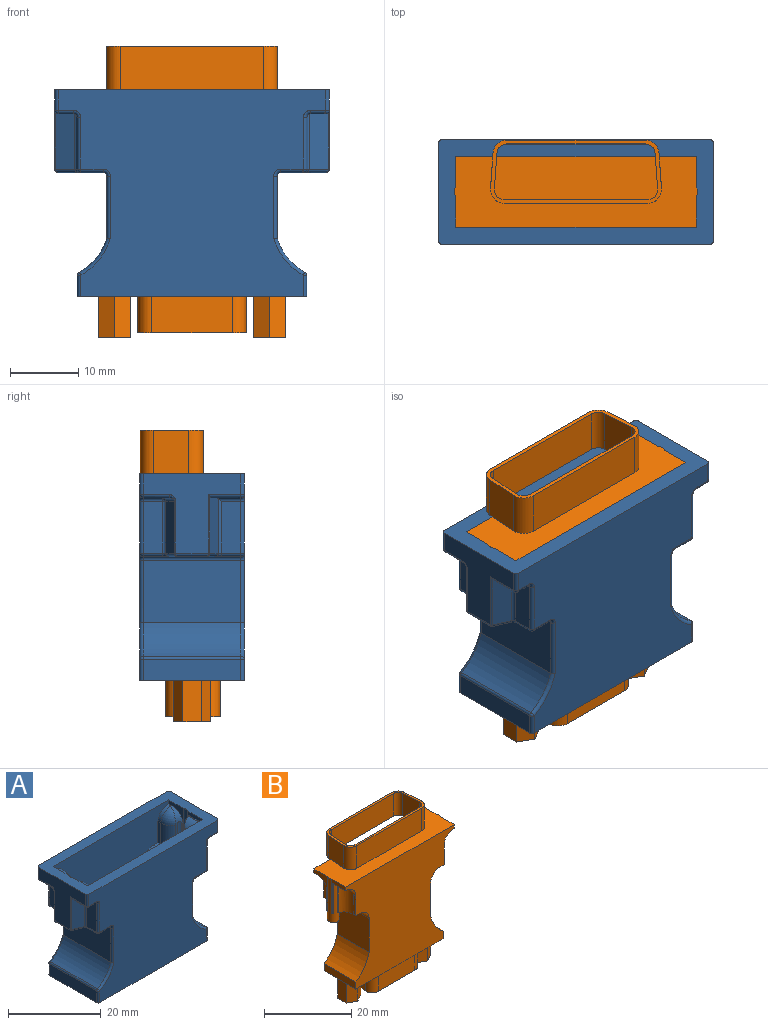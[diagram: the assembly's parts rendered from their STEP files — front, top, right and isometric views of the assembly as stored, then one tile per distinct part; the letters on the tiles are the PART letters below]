
ASSEMBLY  parts=2 mates=1
PART A: 168 faces, bbox 40.4x15.4x30.3 mm
  f0: plane 9.63x4.45mm, normal (-1,0,0), area 8.4mm2, adj f7,f8,f20,f147,f156,f158,f167
  f1: plane 9.63x4.45mm, normal (-1,0,0), area 6.3mm2, adj f2,f5,f20,f146,f154,f167
  f2: plane 0.29x0.24mm, normal (0,0,1), area 0mm2, adj f1,f5,f167
  f3: plane 10.32x3.56mm, normal (0,0,1), area 20.2mm2, adj f4,f6,f146,f147,f153,f157,f161,f164
  f4: plane 8.48x0.4mm, normal (-0.4,0.92,0), area 3.7mm2, adj f3,f9,f165,f167
  f5: plane 8.58x0.24mm, normal (-0.4,0.92,0), area 2.2mm2, adj f1,f2,f154,f167
  f6: plane 5.58x0.4mm, normal (-0.4,-0.92,0), area 2.4mm2, adj f3,f8,f164,f167
  f7: plane 5.58x0.24mm, normal (-0.4,-0.92,0), area 1.4mm2, adj f0,f8,f158,f167
  f8: cylinder r=3mm len=3.38mm, axis (0.92,-0.4,0), area 4.8mm2, adj f0,f6,f7,f156,f163,f167
  f9: cylinder r=3mm len=4.14mm, axis (0,-1,0), area 13.3mm2, adj f4,f146,f153,f154,f165,f167
  f10: plane 9.63x4.45mm, normal (1,0,0), area 6.3mm2, adj f12,f14,f20,f139,f146,f166
  f11: plane 9.63x4.45mm, normal (1,0,0), area 8.4mm2, adj f13,f16,f18,f20,f141,f147,f166
  f12: plane 0.29x0.24mm, normal (0,0,1), area 0mm2, adj f10,f14,f166
  f13: plane 0.29x0.24mm, normal (0,0,1), area 0mm2, adj f11,f16,f166
  f14: plane 8.58x0.24mm, normal (0.4,0.92,0), area 2.2mm2, adj f10,f12,f139,f166
  f15: plane 8.48x0.4mm, normal (0.4,0.92,0), area 3.7mm2, adj f19,f143,f152,f166
  f16: plane 5.58x0.24mm, normal (0.4,-0.92,0), area 1.4mm2, adj f11,f13,f18,f166
  f17: plane 5.58x0.4mm, normal (0.4,-0.92,0), area 2.4mm2, adj f18,f143,f151,f166
  f18: cylinder r=3mm len=3.38mm, axis (-0.92,-0.4,0), area 4.8mm2, adj f11,f16,f17,f141,f150,f166
  f19: cylinder r=3mm len=4.14mm, axis (0,-1,0), area 13.3mm2, adj f15,f138,f139,f146,f152,f166
  f20: plane 40.13x15.32mm, normal (0,0,1), area 251.7mm2, adj f0,f1,f10,f11,f25,f31,f32,f39
  f21: plane 33.5x15.32mm, normal (0,0,-1), area 218.9mm2, adj f24,f31,f32,f37,f40,f83,f94,f97
  f22: plane 7.58x2.89mm, normal (-1,0,0), area 21.9mm2, adj f66,f70,f73,f74
  f23: plane 4.41x2.27mm, normal (0,0,-1), area 8.9mm2, adj f33,f48,f61,f70
  f24: plane 14.32x3.09mm, normal (-1,0,0), area 44.2mm2, adj f21,f37,f40,f41
  f25: plane 14.43x11.74mm, normal (-1,0,0), area 85.1mm2, adj f20,f34,f35,f39,f47,f48,f49,f53
  f26: plane 3.86x2.27mm, normal (0,0,-1), area 7.6mm2, adj f46,f47,f59,f60
  f27: plane 7.58x2.89mm, normal (-1,0,0), area 21.9mm2, adj f58,f59,f68,f69
  f28: plane 14.32x6.62mm, normal (0,0,-1), area 61.4mm2, adj f56,f57,f67,f68,f72,f74,f75,f76
  f29: plane 14.32x9.07mm, normal (-1,0,0), area 129.9mm2, adj f30,f45,f55,f56
  f30: cylinder r=8.49mm len=14.32mm, axis (0,1,0), area 94.5mm2, adj f29,f41,f42,f50
  f31: plane 39.13x30.23mm, normal (0,-1,0), area 887.8mm2, adj f20,f21,f40,f49,f50,f55,f61,f62
  f32: plane 39.13x30.23mm, normal (0,1,0), area 887.8mm2, adj f20,f21,f37,f39,f42,f45,f46,f51
  f33: plane 8.27x2.86mm, normal (-0.4,-0.92,0), area 25mm2, adj f23,f34,f48,f70,f73,f78
  f34: cylinder r=0.2mm len=8.58mm, axis (0,0,1), area 2mm2, adj f25,f33,f48,f80
  f35: cylinder r=0.2mm len=7.58mm, axis (0,0,1), area 1.8mm2, adj f25,f36,f53,f77
  f36: plane 7.58x2.84mm, normal (-0.4,0.92,0), area 23.5mm2, adj f35,f60,f69,f75
  f37: cylinder r=0.5mm len=3.09mm, axis (0,0,-1), area 2.4mm2, adj f21,f24,f32,f38
  f38: sphere r=0.5mm, area 0.2mm2, adj f37,f41,f42
  f39: cylinder r=0.5mm len=3.05mm, axis (0,0,-1), area 2.4mm2, adj f20,f25,f32,f43
  f40: cylinder r=0.5mm len=3.09mm, axis (0,0,1), area 2.4mm2, adj f21,f24,f31,f44
  f41: cylinder r=0.5mm len=14.32mm, axis (0,1,0), area 7.6mm2, adj f24,f30,f38,f44
  f42: torus R=8.99mm, axis (0,-1,0), area 5.3mm2, adj f30,f32,f38,f45
  f43: sphere r=0.5mm, area 0.4mm2, adj f39,f46,f47
  f44: sphere r=0.5mm, area 0.2mm2, adj f40,f41,f50
  f45: cylinder r=0.5mm len=9.14mm, axis (0,0,-1), area 7.2mm2, adj f29,f32,f42,f51
  f46: cylinder r=0.5mm len=2.27mm, axis (1,0,0), area 1.8mm2, adj f26,f32,f43,f52
  f47: cylinder r=0.5mm len=3.86mm, axis (0,1,0), area 3mm2, adj f25,f26,f43,f53
  f48: cylinder r=0.5mm len=4.76mm, axis (0,1,0), area 3.6mm2, adj f23,f25,f33,f34,f54
  f49: cylinder r=0.5mm len=3.05mm, axis (0,0,1), area 2.4mm2, adj f20,f25,f31,f54
  f50: torus R=8.99mm, axis (0,-1,0), area 5.3mm2, adj f30,f31,f44,f55
  f51: torus R=1mm, axis (0,-1,0), area 0.8mm2, adj f32,f45,f56,f57
  f52: torus R=1mm, axis (0,-1,0), area 0.8mm2, adj f32,f46,f58,f59
  f53: bspline ~1x0.89mm, area 0.5mm2, adj f25,f35,f47,f60
  f54: sphere r=0.5mm, area 0.4mm2, adj f48,f49,f61
  f55: cylinder r=0.5mm len=9.14mm, axis (0,0,1), area 7.2mm2, adj f29,f31,f50,f62
  f56: cylinder r=0.5mm len=14.32mm, axis (0,-1,0), area 11.2mm2, adj f28,f29,f51,f62
  f57: cylinder r=0.5mm len=3.35mm, axis (1,0,0), area 2.6mm2, adj f28,f32,f51,f63
  f58: cylinder r=0.5mm len=7.58mm, axis (0,0,-1), area 6mm2, adj f27,f32,f52,f63
  f59: cylinder r=0.5mm len=2.89mm, axis (0,-1,0), area 2.3mm2, adj f26,f27,f52,f64
  f60: cylinder r=0.5mm len=3.04mm, axis (-0.92,-0.4,0), area 2.2mm2, adj f26,f36,f53,f64
  f61: cylinder r=0.5mm len=2.27mm, axis (-1,0,0), area 1.8mm2, adj f23,f31,f54,f65
  f62: torus R=1mm, axis (0,-1,0), area 0.8mm2, adj f31,f55,f56,f67
  f63: sphere r=0.5mm, area 0.4mm2, adj f57,f58,f68
  f64: sphere r=0.5mm, area 0.3mm2, adj f59,f60,f69
  f65: torus R=1mm, axis (0,-1,0), area 0.8mm2, adj f31,f61,f66,f70
  f66: cylinder r=0.5mm len=7.58mm, axis (0,0,1), area 6mm2, adj f22,f31,f65,f71
  f67: cylinder r=0.5mm len=3.35mm, axis (-1,0,0), area 2.6mm2, adj f28,f31,f62,f71
  f68: cylinder r=0.5mm len=2.89mm, axis (0,1,0), area 2.3mm2, adj f27,f28,f63,f72
  f69: cylinder r=0.5mm len=7.58mm, axis (0,0,-1), area 4.4mm2, adj f27,f36,f64,f72
  f70: cylinder r=0.5mm len=3.43mm, axis (0,-1,0), area 2.5mm2, adj f22,f23,f33,f65,f73
  f71: sphere r=0.5mm, area 0.4mm2, adj f66,f67,f74
  f72: torus R=1mm, axis (0,0,1), area 0.6mm2, adj f28,f68,f69,f75
  f73: cylinder r=0.5mm len=8.04mm, axis (0,0,1), area 4.5mm2, adj f22,f33,f70,f76
  f74: cylinder r=0.5mm len=2.89mm, axis (0,1,0), area 2.3mm2, adj f22,f28,f71,f76
  f75: cylinder r=0.5mm len=3.04mm, axis (-0.92,-0.4,0), area 2.4mm2, adj f28,f36,f72,f77
  f76: torus R=1mm, axis (0,0,1), area 0.6mm2, adj f28,f73,f74,f78
  f77: bspline ~0.58x0.5mm, area 0.1mm2, adj f35,f75,f79
  f78: cylinder r=0.5mm len=3.04mm, axis (0.92,-0.4,0), area 2.4mm2, adj f28,f33,f76,f80
  f79: cylinder r=0.5mm len=4.81mm, axis (0,-1,0), area 3.6mm2, adj f25,f28,f77,f80
  f80: bspline ~0.58x0.5mm, area 0.1mm2, adj f34,f78,f79
  f81: plane 7.58x2.89mm, normal (1,0,0), area 21.9mm2, adj f123,f127,f130,f131
  f82: plane 4.41x2.27mm, normal (0,0,-1), area 8.9mm2, adj f90,f105,f118,f127
  f83: plane 14.32x3.09mm, normal (1,0,0), area 44.2mm2, adj f21,f94,f97,f98
  f84: plane 14.43x11.74mm, normal (1,0,0), area 85.1mm2, adj f20,f91,f92,f96,f104,f105,f106,f110
  f85: plane 3.86x2.27mm, normal (0,0,-1), area 7.6mm2, adj f103,f104,f116,f117
  f86: plane 7.58x2.89mm, normal (1,0,0), area 21.9mm2, adj f115,f116,f125,f126
  f87: plane 14.32x6.62mm, normal (0,0,-1), area 61.4mm2, adj f113,f114,f124,f125,f129,f131,f132,f133
  f88: plane 14.32x9.07mm, normal (1,0,0), area 129.9mm2, adj f89,f102,f112,f113
  f89: cylinder r=8.49mm len=14.32mm, axis (0,1,0), area 94.5mm2, adj f88,f98,f99,f107
  f90: plane 8.27x2.86mm, normal (0.4,-0.92,0), area 25mm2, adj f82,f91,f105,f127,f130,f135
  f91: cylinder r=0.2mm len=8.58mm, axis (0,0,1), area 2mm2, adj f84,f90,f105,f137
  f92: cylinder r=0.2mm len=7.58mm, axis (0,0,1), area 1.8mm2, adj f84,f93,f110,f134
  f93: plane 7.58x2.84mm, normal (0.4,0.92,0), area 23.5mm2, adj f92,f117,f126,f132
  f94: cylinder r=0.5mm len=3.09mm, axis (0,0,-1), area 2.4mm2, adj f21,f32,f83,f95
  f95: sphere r=0.5mm, area 0.2mm2, adj f94,f98,f99
  f96: cylinder r=0.5mm len=3.05mm, axis (0,0,-1), area 2.4mm2, adj f20,f32,f84,f100
  f97: cylinder r=0.5mm len=3.09mm, axis (0,0,1), area 2.4mm2, adj f21,f31,f83,f101
  f98: cylinder r=0.5mm len=14.32mm, axis (0,1,0), area 7.6mm2, adj f83,f89,f95,f101
  f99: torus R=8.99mm, axis (0,-1,0), area 5.3mm2, adj f32,f89,f95,f102
  f100: sphere r=0.5mm, area 0.4mm2, adj f96,f103,f104
  f101: sphere r=0.5mm, area 0.2mm2, adj f97,f98,f107
  f102: cylinder r=0.5mm len=9.14mm, axis (0,0,-1), area 7.2mm2, adj f32,f88,f99,f108
  f103: cylinder r=0.5mm len=2.27mm, axis (-1,0,0), area 1.8mm2, adj f32,f85,f100,f109
  f104: cylinder r=0.5mm len=3.86mm, axis (0,1,0), area 3mm2, adj f84,f85,f100,f110
  f105: cylinder r=0.5mm len=4.76mm, axis (0,1,0), area 3.6mm2, adj f82,f84,f90,f91,f111
  f106: cylinder r=0.5mm len=3.05mm, axis (0,0,1), area 2.4mm2, adj f20,f31,f84,f111
  f107: torus R=8.99mm, axis (0,-1,0), area 5.3mm2, adj f31,f89,f101,f112
  f108: torus R=1mm, axis (0,-1,0), area 0.8mm2, adj f32,f102,f113,f114
  f109: torus R=1mm, axis (0,-1,0), area 0.8mm2, adj f32,f103,f115,f116
  f110: bspline ~1x0.89mm, area 0.5mm2, adj f84,f92,f104,f117
  f111: sphere r=0.5mm, area 0.5mm2, adj f105,f106,f118
  f112: cylinder r=0.5mm len=9.14mm, axis (0,0,1), area 7.2mm2, adj f31,f88,f107,f119
  f113: cylinder r=0.5mm len=14.32mm, axis (0,-1,0), area 11.2mm2, adj f87,f88,f108,f119
  f114: cylinder r=0.5mm len=3.35mm, axis (-1,0,0), area 2.6mm2, adj f32,f87,f108,f120
  f115: cylinder r=0.5mm len=7.58mm, axis (0,0,-1), area 6mm2, adj f32,f86,f109,f120
  f116: cylinder r=0.5mm len=2.89mm, axis (0,-1,0), area 2.3mm2, adj f85,f86,f109,f121
  f117: cylinder r=0.5mm len=3.04mm, axis (0.92,-0.4,0), area 2.2mm2, adj f85,f93,f110,f121
  f118: cylinder r=0.5mm len=2.27mm, axis (1,0,0), area 1.8mm2, adj f31,f82,f111,f122
  f119: torus R=1mm, axis (0,-1,0), area 0.8mm2, adj f31,f112,f113,f124
  f120: sphere r=0.5mm, area 0.4mm2, adj f114,f115,f125
  f121: sphere r=0.5mm, area 0.2mm2, adj f116,f117,f126
  f122: torus R=1mm, axis (0,-1,0), area 0.8mm2, adj f31,f118,f123,f127
  f123: cylinder r=0.5mm len=7.58mm, axis (0,0,1), area 6mm2, adj f31,f81,f122,f128
  f124: cylinder r=0.5mm len=3.35mm, axis (1,0,0), area 2.6mm2, adj f31,f87,f119,f128
  f125: cylinder r=0.5mm len=2.89mm, axis (0,1,0), area 2.3mm2, adj f86,f87,f120,f129
  f126: cylinder r=0.5mm len=7.58mm, axis (0,0,-1), area 4.4mm2, adj f86,f93,f121,f129
  f127: cylinder r=0.5mm len=3.43mm, axis (0,-1,0), area 2.5mm2, adj f81,f82,f90,f122,f130
  f128: sphere r=0.5mm, area 0.5mm2, adj f123,f124,f131
  f129: torus R=1mm, axis (0,0,1), area 0.6mm2, adj f87,f125,f126,f132
  f130: cylinder r=0.5mm len=8.04mm, axis (0,0,1), area 4.5mm2, adj f81,f90,f127,f133
  f131: cylinder r=0.5mm len=2.89mm, axis (0,1,0), area 2.3mm2, adj f81,f87,f128,f133
  f132: cylinder r=0.5mm len=3.04mm, axis (0.92,-0.4,0), area 2.4mm2, adj f87,f93,f129,f134
  f133: torus R=1mm, axis (0,0,1), area 0.6mm2, adj f87,f130,f131,f135
  f134: bspline ~0.58x0.5mm, area 0.1mm2, adj f92,f132,f136
  f135: cylinder r=0.5mm len=3.04mm, axis (-0.92,-0.4,0), area 2.4mm2, adj f87,f90,f133,f137
  f136: cylinder r=0.5mm len=4.81mm, axis (0,-1,0), area 3.6mm2, adj f84,f87,f134,f137
  f137: bspline ~0.58x0.5mm, area 0.1mm2, adj f91,f135,f136
  f138: plane 5.58x0.89mm, normal (1,0,0), area 4.9mm2, adj f19,f143,f146,f152
  f139: plane 4.27x0.27mm, normal (0,0,1), area 1.1mm2, adj f10,f14,f19,f146,f166
  f140: plane 10.32x1.98mm, normal (1,0,0), area 20.5mm2, adj f21,f145,f146,f147
  f141: plane 1x0.27mm, normal (0,0,1), area 0.3mm2, adj f11,f18,f147,f149
  f142: plane 5.58x0.89mm, normal (1,0,0), area 4.9mm2, adj f143,f147,f149,f151
  f143: plane 10.32x3.56mm, normal (0,0,1), area 20.2mm2, adj f15,f17,f138,f142,f146,f147,f148,f151
  f144: plane 10.32x9.41mm, normal (1,0,0), area 97.1mm2, adj f145,f146,f147,f148
  f145: cylinder r=10.99mm len=10.32mm, axis (0,1,0), area 79.5mm2, adj f140,f144,f146,f147
  f146: plane 35.13x30.23mm, normal (0,1,0), area 736.9mm2, adj f1,f3,f9,f10,f19,f20,f21,f138
  f147: plane 35.13x30.23mm, normal (0,-1,0), area 736.9mm2, adj f0,f3,f11,f20,f21,f140,f141,f142
  f148: cylinder r=3mm len=10.32mm, axis (0,-1,0), area 48.6mm2, adj f143,f144,f146,f147
  f149: cylinder r=3mm len=3mm, axis (0,-1,0), area 4.2mm2, adj f141,f142,f147,f150
  f150: sphere r=3mm, area 10.5mm2, adj f18,f149,f151
  f151: cylinder r=3mm len=5.58mm, axis (0,0,-1), area 19.5mm2, adj f17,f142,f143,f150
  f152: cylinder r=3mm len=8.33mm, axis (0,0,1), area 24.3mm2, adj f15,f19,f138,f143
  f153: plane 5.58x0.89mm, normal (-1,0,0), area 4.9mm2, adj f3,f9,f146,f165
  f154: plane 4.27x0.27mm, normal (0,0,1), area 1.1mm2, adj f1,f5,f9,f146,f167
  f155: plane 10.32x1.98mm, normal (-1,0,0), area 20.5mm2, adj f21,f146,f147,f160
  f156: plane 1x0.27mm, normal (0,0,1), area 0.3mm2, adj f0,f8,f147,f162
  f157: plane 5.58x0.89mm, normal (-1,0,0), area 4.9mm2, adj f3,f147,f162,f164
  f158: plane 0.29x0.24mm, normal (0,0,1), area 0mm2, adj f0,f7,f167
  f159: plane 10.32x9.41mm, normal (-1,0,0), area 97.1mm2, adj f146,f147,f160,f161
  f160: cylinder r=10.99mm len=10.32mm, axis (0,1,0), area 79.5mm2, adj f146,f147,f155,f159
  f161: cylinder r=3mm len=10.32mm, axis (0,-1,0), area 48.6mm2, adj f3,f146,f147,f159
  f162: cylinder r=3mm len=3mm, axis (0,-1,0), area 4.2mm2, adj f147,f156,f157,f163
  f163: sphere r=3mm, area 11.8mm2, adj f8,f162,f164
  f164: cylinder r=3mm len=5.58mm, axis (0,0,-1), area 19.5mm2, adj f3,f6,f157,f163
  f165: cylinder r=3mm len=8.33mm, axis (0,0,1), area 24.3mm2, adj f3,f4,f9,f153
  f166: cylinder r=1.35mm len=12.13mm, axis (0,0,-1), area 48.8mm2, adj f10,f11,f12,f13,f14,f15,f16,f17
  f167: cylinder r=1.35mm len=12.13mm, axis (0,0,-1), area 48.8mm2, adj f0,f1,f2,f3,f4,f5,f6,f7
PART B: 109 faces, bbox 37.5x12.7x42.6 mm
  f0: plane 23.86x6.27mm, normal (0,0,1), area 147.2mm2, adj f32,f92,f93,f97,f98,f107
  f1: plane 28.5x10.32mm, normal (0,0,-1), area 136.3mm2, adj f25,f31,f32,f40,f55,f56,f57,f58
  f2: plane 2.7x2.7mm, normal (0,0,-1), area 5.7mm2, adj f52
  f3: plane 9.63x4.45mm, normal (1,0,0), area 8.4mm2, adj f10,f11,f32,f41,f43,f52,f54
  f4: plane 9.63x4.45mm, normal (1,0,0), area 6.3mm2, adj f5,f8,f31,f39,f52,f54
  f5: plane 0.29x0.24mm, normal (0,0,-1), area 0mm2, adj f4,f8,f52
  f6: plane 10.32x3.56mm, normal (0,0,-1), area 20.2mm2, adj f7,f9,f31,f32,f38,f42,f46,f49
  f7: plane 8.48x0.4mm, normal (0.4,-0.92,0), area 3.7mm2, adj f6,f12,f50,f52
  f8: plane 8.58x0.24mm, normal (0.4,-0.92,0), area 2.2mm2, adj f4,f5,f39,f52
  f9: plane 5.58x0.4mm, normal (0.4,0.92,0), area 2.4mm2, adj f6,f11,f49,f52
  f10: plane 5.58x0.24mm, normal (0.4,0.92,0), area 1.4mm2, adj f3,f11,f43,f52
  f11: cylinder r=3mm len=3.38mm, axis (0.92,-0.4,0), area 4.8mm2, adj f3,f9,f10,f41,f48,f52
  f12: cylinder r=3mm len=4.14mm, axis (0,-1,0), area 13.2mm2, adj f7,f31,f38,f39,f50,f52
  f13: plane 9.63x4.45mm, normal (-1,0,0), area 6.3mm2, adj f15,f17,f24,f31,f51,f54
  f14: plane 9.63x4.45mm, normal (-1,0,0), area 8.4mm2, adj f16,f19,f21,f26,f32,f51,f54
  f15: plane 0.29x0.24mm, normal (0,0,-1), area 0mm2, adj f13,f17,f51
  f16: plane 0.29x0.24mm, normal (0,0,-1), area 0mm2, adj f14,f19,f51
  f17: plane 8.58x0.24mm, normal (-0.4,-0.92,0), area 2.2mm2, adj f13,f15,f24,f51
  f18: plane 8.48x0.4mm, normal (-0.4,-0.92,0), area 3.7mm2, adj f22,f28,f37,f51
  f19: plane 5.58x0.24mm, normal (-0.4,0.92,0), area 1.4mm2, adj f14,f16,f21,f51
  f20: plane 5.58x0.4mm, normal (-0.4,0.92,0), area 2.4mm2, adj f21,f28,f36,f51
  f21: cylinder r=3mm len=3.38mm, axis (-0.92,-0.4,0), area 4.8mm2, adj f14,f19,f20,f26,f35,f51
  f22: cylinder r=3mm len=4.14mm, axis (0,-1,0), area 13.2mm2, adj f18,f23,f24,f31,f37,f51
  f23: plane 5.58x0.89mm, normal (-1,0,0), area 4.9mm2, adj f22,f28,f31,f37
  f24: plane 4.27x0.27mm, normal (0,0,-1), area 1.1mm2, adj f13,f17,f22,f31,f51
  f25: plane 10.32x1.98mm, normal (-1,0,0), area 20.5mm2, adj f1,f30,f31,f32
  f26: plane 1x0.27mm, normal (0,0,-1), area 0.3mm2, adj f14,f21,f32,f34
  f27: plane 5.58x0.89mm, normal (-1,0,0), area 4.9mm2, adj f28,f32,f34,f36
  f28: plane 10.32x3.56mm, normal (0,0,-1), area 20.2mm2, adj f18,f20,f23,f27,f31,f32,f33,f36
  f29: plane 10.32x9.41mm, normal (-1,0,0), area 97.1mm2, adj f30,f31,f32,f33
  f30: cylinder r=10.99mm len=10.32mm, axis (0,1,0), area 79.5mm2, adj f25,f29,f31,f32
  f31: plane 35.13x30.23mm, normal (0,-1,0), area 736.9mm2, adj f1,f4,f6,f12,f13,f22,f23,f24
  f32: plane 35.13x30.23mm, normal (0,1,0), area 736.9mm2, adj f0,f1,f3,f6,f14,f25,f26,f27
  f33: cylinder r=3mm len=10.32mm, axis (0,-1,0), area 48.6mm2, adj f28,f29,f31,f32
  f34: cylinder r=3mm len=3mm, axis (0,-1,0), area 4.2mm2, adj f26,f27,f32,f35
  f35: sphere r=3mm, area 10.5mm2, adj f21,f34,f36
  f36: cylinder r=3mm len=5.58mm, axis (0,0,-1), area 19.5mm2, adj f20,f27,f28,f35
  f37: cylinder r=3mm len=8.33mm, axis (0,0,1), area 24.9mm2, adj f18,f22,f23,f28
  f38: plane 5.58x0.89mm, normal (1,0,0), area 4.9mm2, adj f6,f12,f31,f50
  f39: plane 4.27x0.27mm, normal (0,0,-1), area 1.1mm2, adj f4,f8,f12,f31,f52
  f40: plane 10.32x1.98mm, normal (1,0,0), area 20.5mm2, adj f1,f31,f32,f45
  f41: plane 1x0.27mm, normal (0,0,-1), area 0.3mm2, adj f3,f11,f32,f47
  f42: plane 5.58x0.89mm, normal (1,0,0), area 4.9mm2, adj f6,f32,f47,f49
  f43: plane 0.29x0.24mm, normal (0,0,-1), area 0mm2, adj f3,f10,f52
  f44: plane 10.32x9.41mm, normal (1,0,0), area 97.1mm2, adj f31,f32,f45,f46
  f45: cylinder r=10.99mm len=10.32mm, axis (0,1,0), area 79.5mm2, adj f31,f32,f40,f44
  f46: cylinder r=3mm len=10.32mm, axis (0,-1,0), area 48.6mm2, adj f6,f31,f32,f44
  f47: cylinder r=3mm len=3mm, axis (0,-1,0), area 4.2mm2, adj f32,f41,f42,f48
  f48: sphere r=3mm, area 10.5mm2, adj f11,f47,f49
  f49: cylinder r=3mm len=5.58mm, axis (0,0,-1), area 19.5mm2, adj f6,f9,f42,f48
  f50: cylinder r=3mm len=8.33mm, axis (0,0,1), area 24.9mm2, adj f6,f7,f12,f38
  f51: cylinder r=1.35mm len=12.13mm, axis (0,0,-1), area 48.8mm2, adj f13,f14,f15,f16,f17,f18,f19,f20
  f52: cylinder r=1.35mm len=12.13mm, axis (0,0,-1), area 48.8mm2, adj f2,f3,f4,f5,f6,f7,f8,f9
  f53: plane 2.7x2.7mm, normal (0,0,-1), area 5.7mm2, adj f51
  f54: plane 35.53x10.32mm, normal (0,0,1), area 195.2mm2, adj f3,f4,f13,f14,f31,f32,f51,f52
  f55: plane 6.05x2.38mm, normal (-0.5,-0.87,0), area 16.6mm2, adj f1,f56,f60,f61
  f56: plane 6.05x2.74mm, normal (-1,0,0), area 16.6mm2, adj f1,f55,f57,f61
  f57: plane 6.05x2.38mm, normal (-0.5,0.87,0), area 16.6mm2, adj f1,f56,f58,f61
  f58: plane 6.05x2.38mm, normal (0.5,0.87,0), area 16.6mm2, adj f1,f57,f59,f61
  f59: plane 6.05x2.74mm, normal (1,0,0), area 16.6mm2, adj f1,f58,f60,f61
  f60: plane 6.05x2.38mm, normal (0.5,-0.87,0), area 16.6mm2, adj f1,f55,f59,f61
  f61: plane 5.49x4.75mm, normal (0,0,-1), area 14.4mm2, adj f55,f56,f57,f58,f59,f60,f71
  f62: plane 6.05x2.38mm, normal (-0.5,0.87,0), area 16.6mm2, adj f1,f63,f67,f68
  f63: plane 6.05x2.38mm, normal (0.5,0.87,0), area 16.6mm2, adj f1,f62,f64,f68
  f64: plane 6.05x2.74mm, normal (1,0,0), area 16.6mm2, adj f1,f63,f65,f68
  f65: plane 6.05x2.38mm, normal (0.5,-0.87,0), area 16.6mm2, adj f1,f64,f66,f68
  f66: plane 6.05x2.38mm, normal (-0.5,-0.87,0), area 16.6mm2, adj f1,f65,f67,f68
  f67: plane 6.05x2.74mm, normal (-1,0,0), area 16.6mm2, adj f1,f62,f66,f68
  f68: plane 5.49x4.75mm, normal (0,0,-1), area 14.4mm2, adj f62,f63,f64,f65,f66,f67,f69
  f69: cylinder r=1.28mm len=3.16mm, axis (0,0,-1), area 25.3mm2, adj f68,f70
  f70: plane 2.55x2.55mm, normal (0,0,-1), area 5.1mm2, adj f69
  f71: cylinder r=1.28mm len=3.16mm, axis (0,0,-1), area 25.3mm2, adj f61,f72
  f72: plane 2.55x2.55mm, normal (0,0,-1), area 5.1mm2, adj f71
  f73: plane 11.8x5.32mm, normal (0,-1,0), area 62.8mm2, adj f1,f74,f88,f89
  f74: cylinder r=2mm len=5.32mm, axis (0,0,1), area 17.9mm2, adj f1,f73,f75,f89
  f75: plane 5.32x3.95mm, normal (-0.99,0.11,0), area 21.1mm2, adj f1,f74,f76,f89
  f76: cylinder r=2mm len=5.32mm, axis (0,0,1), area 15.5mm2, adj f1,f75,f77,f89
  f77: plane 10.91x5.32mm, normal (0,1,0), area 58.1mm2, adj f1,f76,f78,f89
  f78: cylinder r=2mm len=5.32mm, axis (0,0,1), area 15.5mm2, adj f1,f77,f79,f89
  f79: plane 5.32x3.95mm, normal (0.99,0.11,0), area 21.1mm2, adj f1,f78,f88,f89
  f80: cylinder r=0.91mm len=5.32mm, axis (0,0,1), area 8.1mm2, adj f81,f87,f89,f90
  f81: plane 11.8x5.32mm, normal (0,1,0), area 62.8mm2, adj f80,f82,f89,f90
  f82: cylinder r=0.91mm len=5.32mm, axis (0,0,1), area 8.1mm2, adj f81,f83,f89,f90
  f83: plane 5.32x3.95mm, normal (-0.99,-0.11,0), area 21.1mm2, adj f82,f84,f89,f90
  f84: cylinder r=0.91mm len=5.32mm, axis (0,0,1), area 7.1mm2, adj f83,f85,f89,f90
  f85: plane 10.91x5.32mm, normal (0,-1,0), area 58.1mm2, adj f84,f86,f89,f90
  f86: cylinder r=0.91mm len=5.32mm, axis (0,0,1), area 7.1mm2, adj f85,f87,f89,f90
  f87: plane 5.32x3.95mm, normal (0.99,-0.11,0), area 21.1mm2, adj f80,f86,f89,f90
  f88: cylinder r=2mm len=5.32mm, axis (0,0,1), area 17.9mm2, adj f1,f73,f79,f89
  f89: plane 15.8x7.95mm, normal (0,0,-1), area 43.4mm2, adj f73,f74,f75,f76,f77,f78,f79,f80
  f90: plane 13.62x5.77mm, normal (0,0,-1), area 75.4mm2, adj f80,f81,f82,f83,f84,f85,f86,f87
  f91: plane 24.33x2.39mm, normal (0,0,-1), area 15.1mm2, adj f32,f93,f94,f95,f96,f97,f99,f103
  f92: cylinder r=1.43mm len=6.35mm, axis (0,0,-1), area 14.9mm2, adj f0,f93,f107,f108
  f93: plane 6.35x5.23mm, normal (1,-0.07,0), area 33.3mm2, adj f0,f91,f92,f94,f108
  f94: cylinder r=1.43mm len=6.35mm, axis (0,0,-1), area 13.6mm2, adj f91,f93,f95,f108
  f95: plane 20.27x6.35mm, normal (0,-1,0), area 128.7mm2, adj f91,f94,f96,f108
  f96: cylinder r=1.43mm len=6.35mm, axis (0,0,-1), area 13.6mm2, adj f91,f95,f97,f108
  f97: plane 6.35x5.23mm, normal (-1,-0.07,0), area 33.3mm2, adj f0,f91,f96,f98,f108
  f98: cylinder r=1.43mm len=6.35mm, axis (0,0,-1), area 14.9mm2, adj f0,f97,f107,f108
  f99: plane 6.35x5.23mm, normal (-1,0.07,0), area 33.3mm2, adj f54,f91,f100,f106,f108
  f100: cylinder r=2mm len=6.35mm, axis (0,0,-1), area 20.8mm2, adj f54,f99,f101,f108
  f101: plane 21x6.35mm, normal (0,-1,0), area 133.4mm2, adj f54,f100,f102,f108
  f102: cylinder r=2mm len=6.35mm, axis (0,0,-1), area 20.8mm2, adj f54,f101,f103,f108
  f103: plane 6.35x5.23mm, normal (1,0.07,0), area 33.3mm2, adj f54,f91,f102,f104,f108
  f104: cylinder r=2mm len=6.35mm, axis (0,0,-1), area 19.1mm2, adj f91,f103,f105,f108
  f105: plane 20.27x6.35mm, normal (0,1,0), area 128.7mm2, adj f91,f104,f106,f108
  f106: cylinder r=2mm len=6.35mm, axis (0,0,-1), area 19.1mm2, adj f91,f99,f105,f108
  f107: plane 21x6.35mm, normal (0,1,0), area 133.4mm2, adj f0,f92,f98,f108
  f108: plane 25x9.23mm, normal (0,0,1), area 35.6mm2, adj f92,f93,f94,f95,f96,f97,f98,f99
PLACE A t=(3.31,31.05,-4.38)mm
PLACE B t=(3.31,31.05,-4.38)mm
MATE fastened B.f54 <-> A.f20  axis (0,0,1) through (-14.26,28.55,45.2)mm
